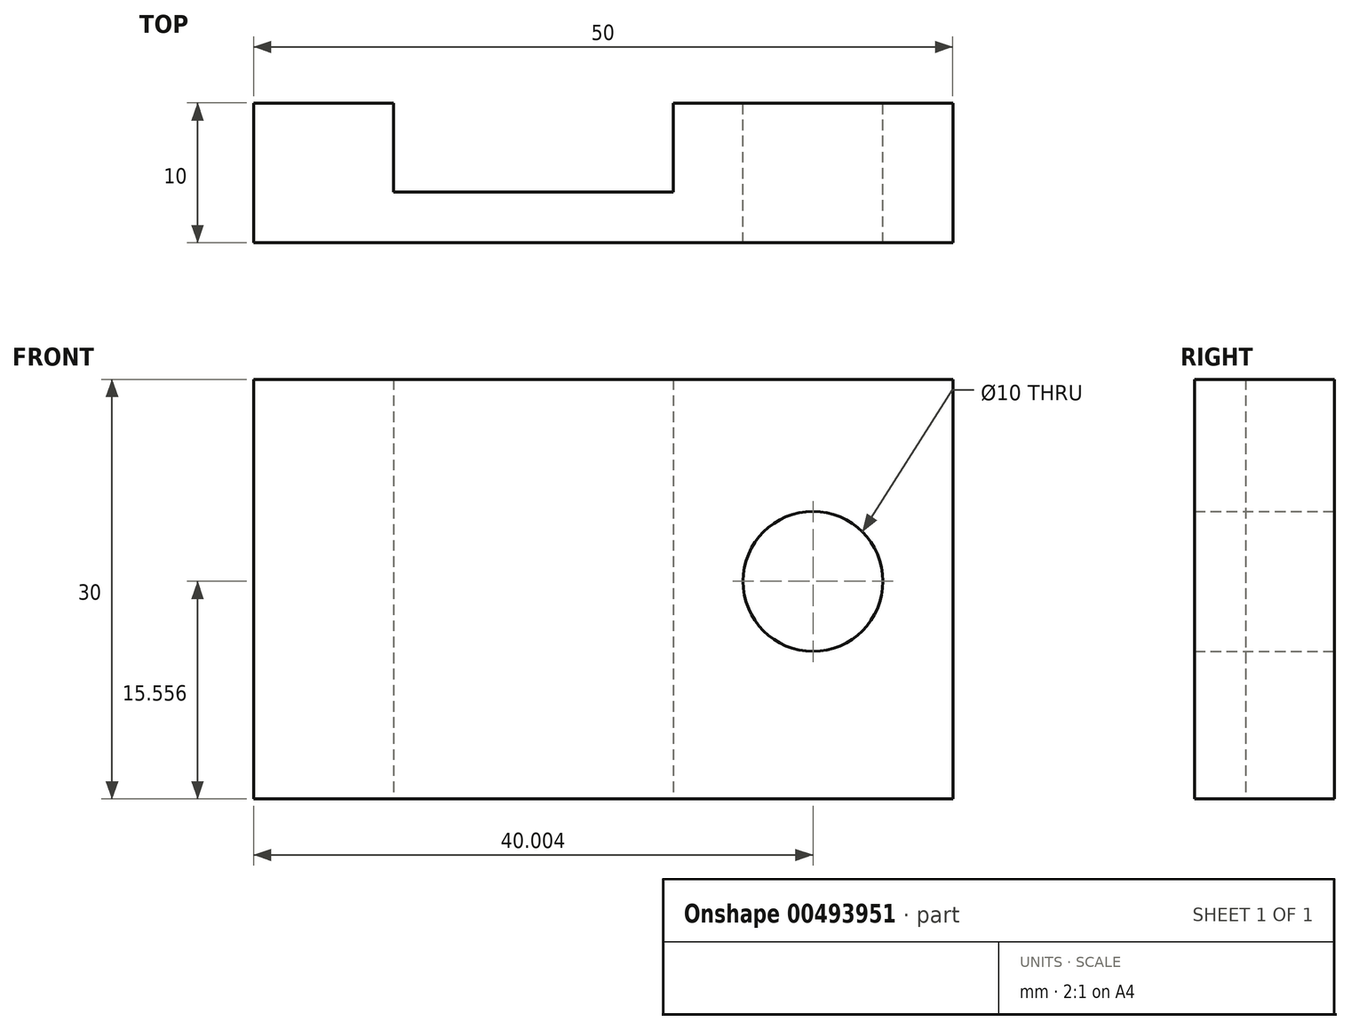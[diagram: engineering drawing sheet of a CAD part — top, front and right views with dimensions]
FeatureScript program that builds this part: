
annotation { "Feature Type Name" : "Feature", "Feature Type Description" : "" }
export const myFeature = defineFeature(function(context is Context, id is Id, definition is map)
    precondition{}
    {
        {
            var Q0;
            Q0=qCreatedBy(makeId("Top.planeOp"),FACE);
            var sketch = newSketch(context, id + "F0", { "sketchPlane" : qUnion([Q0])});
            skLineSegment(sketch, "E0", {"start": v(-15.62, -6.8) * mm, "end": v(34.38, -6.8) * mm});
            skLineSegment(sketch, "E1", {"start": v(34.38, -6.8) * mm, "end": v(34.38, 3.2) * mm});
            skLineSegment(sketch, "E2", {"start": v(34.38, 3.2) * mm, "end": v(14.38, 3.2) * mm});
            skLineSegment(sketch, "E3", {"start": v(14.38, 3.2) * mm, "end": v(14.38, -3.16) * mm});
            skLineSegment(sketch, "E4", {"start": v(14.38, -3.16) * mm, "end": v(-5.62, -3.16) * mm});
            skLineSegment(sketch, "E5", {"start": v(-5.62, -3.16) * mm, "end": v(-5.62, 3.2) * mm});
            skLineSegment(sketch, "E6", {"start": v(-5.62, 3.2) * mm, "end": v(-15.62, 3.2) * mm});
            skLineSegment(sketch, "E7", {"start": v(-15.62, 3.2) * mm, "end": v(-15.62, -6.8) * mm});
            skSolve(sketch);
        }
        {
            var Q0;
            Q0=makeQuery(id+"F0.imprint","IMPRINT",FACE,{"disambiguationData":[TD([[makeQuery(id+"F0.imprint","IMPRINT",EDGE,{"derivedFrom":sQuery(id+"F0.wireOp",EDGE,"E0")}),1.0]])]});
            extrude(context, id + "F1", {"entities" : qUnion([Q0]), "depth" : 30 * mm});
        }
        {
            var Q0;
            Q0=makeQuery(id+"F1.opExtrude","SWEPT_FACE",FACE,{"disambiguationData":[OSD([sQuery(id+"F0.wireOp",EDGE,"E2")])]});
            var sketch = newSketch(context, id + "F2", { "sketchPlane" : qUnion([Q0])});
            skPoint(sketch, "E8", {"position": v(-24.38, 15.56) * mm});
            skCircle(sketch, "E9", {"center": v(-24.38, 15.56) * mm, "radius": 5 * mm});
            skSolve(sketch);
        }
        {
            var Q0;
            Q0=sQuery(id+"F2.wireOp",VERTEX,"E8");
            var Q1;
            Q1=makeQuery(id+"F1.opExtrude","SWEPT_BODY",BODY,{"disambiguationData":[OSD([sQuery(id+"F0.wireOp",EDGE,"E0"),sQuery(id+"F0.wireOp",EDGE,"E1"),sQuery(id+"F0.wireOp",EDGE,"E2"),sQuery(id+"F0.wireOp",EDGE,"E3"),sQuery(id+"F0.wireOp",EDGE,"E4"),sQuery(id+"F0.wireOp",EDGE,"E5"),sQuery(id+"F0.wireOp",EDGE,"E6"),sQuery(id+"F0.wireOp",EDGE,"E7")])]});
            hole(context, id + "F3", {"style" : HoleStyle.SIMPLE, "endStyle" : HoleEndStyle.THROUGH, "holeDiameter" : 10 * mm, "isTappedThrough" : true, "tappedDepth" : 12 * mm, "tapClearance" : 3, "locations" : qUnion([Q0]), "scope" : qUnion([Q1])});
        }
    });
